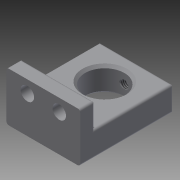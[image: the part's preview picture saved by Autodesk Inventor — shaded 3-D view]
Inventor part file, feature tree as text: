
AUTODESK INVENTOR PART (.ipt)
format: ipt  version: 2014 SP2 (Build 180246200, 246)  size: 207,872 bytes
history: native  units: mm
features: sketch x11, extrude x7, other x7, revolve x2, hole x2, thread x1
ambient origin geometry x8: Origin, YZ Plane, XZ Plane, XY Plane, X Axis, Y Axis, Z Axis, Center Point
bodies: Solid1 (feature_tree)
feature tree (30):
  sketch  "Sketch_9"
  sketch  "Sketch_10"
  extrude  "Extrusion1"  Depth=38.0mm TaperAngle=0.0deg
  extrude  "Extrusion2"  TaperAngle=360.0deg  [1 undecoded]
  extrude  "Extrusion3"  Depth=4.621mm TaperAngle=0.0deg
  revolve  "Revolution1"  [1 undecoded]
  revolve  "Revolution2"  [1 undecoded]
  thread  "Thread1"  [1 undecoded]
  hole  "Hole1"  [1 undecoded]
  hole  "Hole2"  [1 undecoded]
  extrude  "Extrusion4"  [1 undecoded]
  extrude  "Extrusion5"  [1 undecoded]
  extrude  "Extrusion6"  [1 undecoded]
  extrude  "Extrusion7"  [1 undecoded]
  other  "b_s_XY"
  other  "b_s_YZ"
  other  "b_s_ZX"
  other  "b_s_X"
  other  "b_s_Y"
  other  "b_s_Z"
  other  "b_s_Center"
  sketch  "Sketch_5"  dims[d7=360.0deg d8=4.621mm d9=0.0mm]
  sketch  "Sketch_7"  dims[d26=0.8mm d27=0.0mm d28=30.0mm d29=0.0mm d30=28.0mm d31=0.0mm]
  sketch  "Sketch_1"  dims[d0=20.0mm d1=0.0mm d2=38.0mm d3=0.0mm]
  sketch  "Sketch6"  dims[d10=5.5mm d11=6.0mm d12=6.5mm d13=2.0mm d14=90.0deg d15=6.0mm d16=0.0mm]
  sketch  "Sketch7"  dims[d32=0.0mm]
  sketch  "Sketch_4"  dims[d4=10.0mm d5=0.0mm d6=360.0deg]
  sketch  "Sketch_8"
  sketch  "Sketch_6"  dims[d17=5.5mm d18=6.0mm d19=6.5mm d20=2.0mm d21=90.0deg d22=6.0mm d23=0.0mm d24=38.0mm d25=0.0mm]
  sketch  "Sketch_11"
note: 10 required parameter values undecoded (feature->parameter linkage not recoverable at this tier; creation-order binding heuristic only, values carry confidence <= 0.55)